# Revit family: Drain_Floor-Jay R.Smith-Round-Type-DX2312_Series
name_source: partatom
category: Plumbing Fixtures
units: mm (PartAtom-declared; Revit-internal decimal feet)

## family parameters
Always vertical = Yes
Cut with Voids When Loaded = No
OmniClass Number = 23.70.50.21.24
OmniClass Title = Waste Water Drains
Part Type = Normal
Room Calculation Point = No
Round Connector Dimension = Use Radius
Shared = No
Work Plane-Based = Yes

## types (12) — shared parameters
Adjustable Height = 3/16"
Adjustable Height Constraint = 3/16"
Assembly Code = D2030300
CW Connection = No
Default Elevation = 0"
Description = Floor Drain with Adjustable Lip Dimension
Diameter = 17"
Finish = Cast Iron-Jay R Smith-Duco Coated
G - Galvanized Cast Iron = No
HW Connection = No
Load Rating = 'Light Duty having a Safe Live (Static) Load less than 2,000 lbs. (900 kg) per ASME A112.6.3 Floor Drain Standard.
Manufacturer = Jay R. Smith
Material = Cast Iron-Jay R Smith-Duco Coated
NB - Nickel Bronze Top = No
NO-HUB Adaptor = No
PB - Polished Bronze Top = No
Product Documentation Link = https://www.jrsmith.com
Product Page URL = https://www.jrsmith.com
Quad Close Trap Seal = No
SH - Securing Holes = No
Strainer Diameter = 8 1/2"
T - Threaded Outlet = No
U - Vandal Proof Grate = No
URL = http://www.jrsmith.com
Vent Connection = No
Waste Connection = Yes

## per-type parameters (varying)
| type | Body Height | Connection Radius | Connection Size | Height | Outlet Connection Description | Type Comments |
| DX2312C 02 | 4 1/2" | 1" | 2" | 4 11/16" | 2" Caulk Outlet Connection | Less Bucket |
| DX2312C 03 | 4 1/2" | 1 1/2" | 3" | 4 11/16" | 3" Caulk Outlet Connection | Less Bucket |
| DX2312C 04 | 4 1/2" | 2" | 4" | 4 11/16" | 4" Caulk Outlet Connection | Less Bucket |
| DX2312CB 02 | 4 1/2" | 1" | 2" | 4 11/16" | 2" Caulk Outlet Connection | Safe Set Bucket |
| DX2312CB 03 | 4 1/2" | 1 1/2" | 3" | 4 11/16" | 3" Caulk Outlet Connection | Safe Set Bucket |
| DX2312CB 04 | 4 1/2" | 2" | 4" | 4 11/16" | 4" Caulk Outlet Connection | Safe Set Bucket |
| DX2312T 02 | 3 1/2" | 1" | 2" | 3 11/16" | 2" Threaded Outlet Connection | Less Bucket |
| DX2312T 03 | 3 1/2" | 1 1/2" | 3" | 3 11/16" | 3" Threaded Outlet Connection | Less Bucket |
| DX2312T 04 | 3 1/2" | 2" | 4" | 3 11/16" | 4" Threaded Outlet Connection | Less Bucket |
| DX2312TB 02 | 3 1/2" | 1" | 2" | 3 11/16" | 2" Threaded Outlet Connection | Safe Set Bucket |
| DX2312TB 03 | 3 1/2" | 1 1/2" | 3" | 3 11/16" | 3" Threaded Outlet Connection | Safe Set Bucket |
| DX2312TB 04 | 3 1/2" | 2" | 4" | 3 11/16" | 4" Threaded Outlet Connection | Safe Set Bucket |

note: column(s) folded — value = type name in every type: Model

## geometry (parser evidence)
native form markers: Sweep x3
no freeform markers — native parametric forms only
